# Revit family: 191216_01_AIRTECNICS_AIR CURTAIN_COMPACT FLY_AIR ONLY (A)
name_source: partatom
category: Mechanical Equipment
revit_build: Autodesk Revit 2016 (Build: 20150714_1515(x64)
units: mm (PartAtom-declared; Revit-internal decimal feet)

## family parameters
Always vertical = Yes
Cut with Voids When Loaded = No
OmniClass Number = 23.75.70.21.17
OmniClass Title = Air Curtains
Part Type = Normal
Room Calculation Point = No
Round Connector Dimension = Use Diameter
Shared = No
Work Plane-Based = No

## types (2) — shared parameters
A = Yes
BIMETRICAL = http://www.bimetrical.com
BIMETRICAL Category = Fan
Depth = 220 mm
Family Version = 1.0
Fans Stage = 2
Frequency = 50 Hz
Height = 250 mm
IfcExportAs = IfcFanType
IfcExportType = CENTRIFUGALFORWARDCURVED
Manufacturer = AIRTECNICS
Model = Air Curtain Compact Fly A
Name_Lookup_Data = COMPACT FLY_(A)_Data_Lookup
Review Date = 12/19
Revit Version = Revit 2016 - English
Type Comments = Specially designed for insects control at windows such as food establishments and industry, tollbooth and kiosks.
High velocity air barrier to prevent flying insects from entering a building.
Valid for service windows according to NSF 37 standard.
Self-supporting casing construction made of galvanized steel plate, finished in structural epoxy-polyester painting white colour RAL9016 as standard. Other colours or stainless steel are available on request.
Large faceted inlet grille avoiding intensive maintenance.
Anodized aluminium outlet vanes, airfoil shaped, adjustable in both directions.
Double-inlet centrifugal fans driven by an external rotor motor and low noise level. 2-speed selector (confort mode and fly mode).
“A” type without heating, air only.
Included regulation with infrared remote control and inbuilt keypad with leds.
Type Image = <None>
URL = https://www.airtecnics.com
URL_Datasheet = https://www.airtecnics.com
URL_Manufacturer = https://www.airtecnics.com
· HEATING · = -/ Select Heating /-

## per-type parameters (varying)
| type | COD | L | Length | Product Size |
| COMPACT FLY 600 A | 2 | 600 mm | 630 mm  [stored 2.06693 ft] | 600 |
| COMPACT FLY 900 A | 4 | 900 mm | 930 mm | 900 |

note: [stored X ft] marks values corroborated as IEEE doubles in the binary element streams (Revit-internal decimal feet)

## geometry (parser evidence)
native form markers: Blend x2
no freeform markers — native parametric forms only
